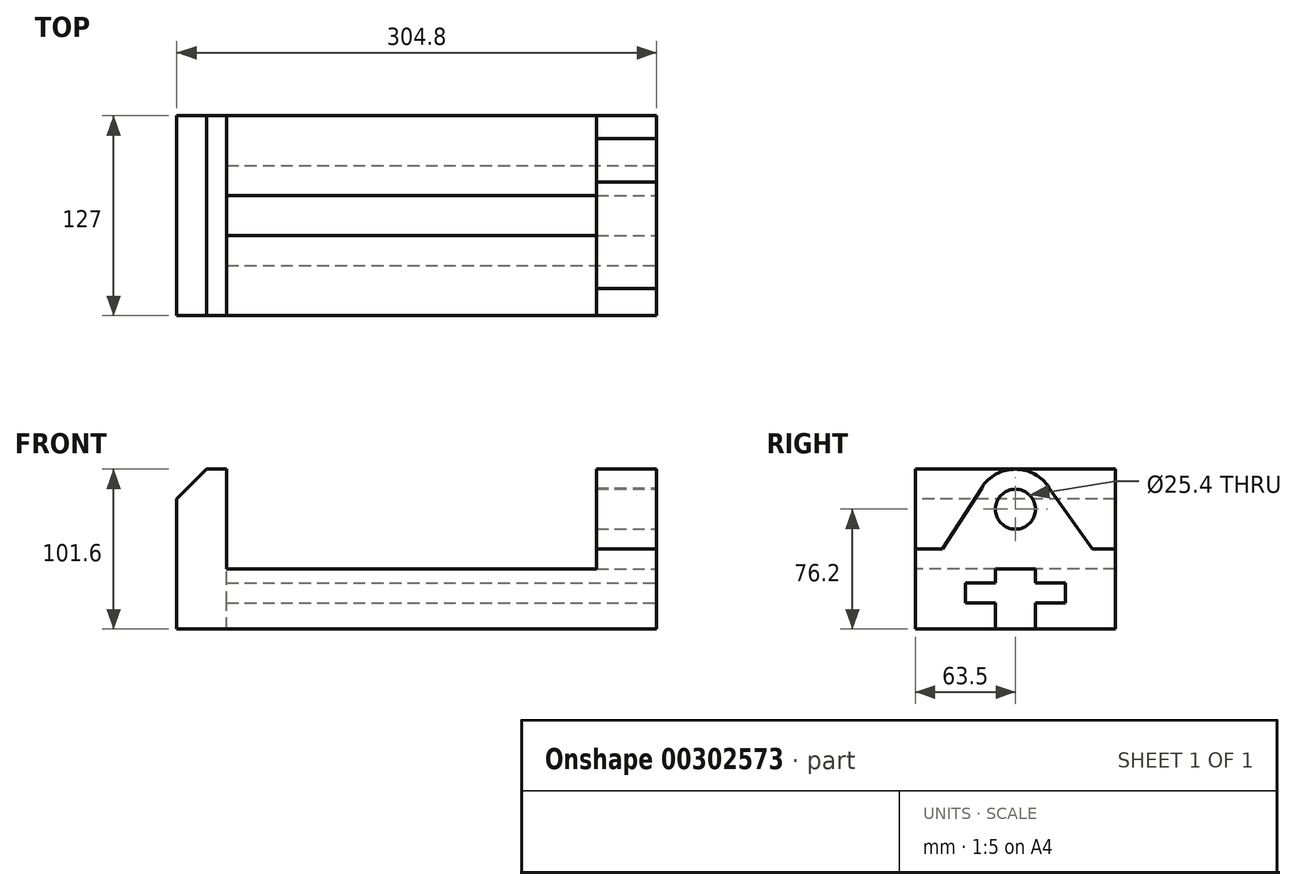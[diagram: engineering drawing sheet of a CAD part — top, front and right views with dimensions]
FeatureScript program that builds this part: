
annotation { "Feature Type Name" : "Feature", "Feature Type Description" : "" }
export const myFeature = defineFeature(function(context is Context, id is Id, definition is map)
    precondition{}
    {
        {
            var Q0;
            Q0=qCreatedBy(makeId("Front.planeOp"),FACE);
            var sketch = newSketch(context, id + "F0", { "sketchPlane" : qUnion([Q0])});
            skLineSegment(sketch, "E0.bottom", {"start": v(0, 0) * mm, "end": v(304.8, 0) * mm});
            skLineSegment(sketch, "E0.top", {"start": v(0, 101.6) * mm, "end": v(304.8, 101.6) * mm});
            skLineSegment(sketch, "E0.left", {"start": v(0, 0) * mm, "end": v(0, 101.6) * mm});
            skLineSegment(sketch, "E0.right", {"start": v(304.8, 0) * mm, "end": v(304.8, 101.6) * mm});
            skSolve(sketch);
        }
        {
            var Q0;
            Q0 = qSketchRegion(id + "F0", true);
            extrude(context, id + "F1", {"entities" : qUnion([Q0]), "oppositeDirection" : true, "depth" : 127 * mm});
        }
        {
            var Q0;
            Q0=makeQuery(id+"F1.opExtrude","CAP_FACE",FACE,{"disambiguationData":[OSD([sQuery(id+"F0.wireOp",EDGE,"E0.bottom"),sQuery(id+"F0.wireOp",EDGE,"E0.top"),sQuery(id+"F0.wireOp",EDGE,"E0.left"),sQuery(id+"F0.wireOp",EDGE,"E0.right")])],"isStart":true});
            var sketch = newSketch(context, id + "F2", { "sketchPlane" : qUnion([Q0])});
            skLineSegment(sketch, "E1", {"start": v(0, 101.6) * mm, "end": v(31.75, 101.6) * mm});
            skLineSegment(sketch, "E2", {"start": v(304.8, 101.6) * mm, "end": v(266.7, 101.6) * mm});
            skLineSegment(sketch, "E3", {"start": v(0, 38.1) * mm, "end": v(304.8, 38.1) * mm, "construction": true});
            skLineSegment(sketch, "E4", {"start": v(31.75, 101.6) * mm, "end": v(31.75, 38.1) * mm});
            skLineSegment(sketch, "E5", {"start": v(31.75, 38.1) * mm, "end": v(266.7, 38.1) * mm});
            skLineSegment(sketch, "E6", {"start": v(266.7, 38.1) * mm, "end": v(266.7, 101.6) * mm});
            skSolve(sketch);
        }
        {
            var Q0;
            {var subQ0=sQuery(id+"F2.wireOp",EDGE,"E4");Q0=makeQuery(id+"F2.imprint","IMPRINT",FACE,{"disambiguationData":[TD([[makeQuery(id+"F2.imprint","IMPRINT",EDGE,{"derivedFrom":subQ0}),1.0]])]});}
            extrude(context, id + "F3", {"entities" : qUnion([Q0]), "operationType" : NewBodyOperationType.REMOVE, "endBound" : BoundingType.THROUGH_ALL, "oppositeDirection" : true, "depth" : 25.4 * mm});
        }
        {
            var Q0;
            Q0=makeQuery(id+"F1.opExtrude","CAP_FACE",FACE,{"disambiguationData":[OSD([sQuery(id+"F0.wireOp",EDGE,"E0.bottom"),sQuery(id+"F0.wireOp",EDGE,"E0.top"),sQuery(id+"F0.wireOp",EDGE,"E0.left"),sQuery(id+"F0.wireOp",EDGE,"E0.right")])],"isStart":true});
            var sketch = newSketch(context, id + "F4", { "sketchPlane" : qUnion([Q0])});
            skLineSegment(sketch, "E7", {"start": v(0, 101.6) * mm, "end": v(19.05, 101.6) * mm});
            skLineSegment(sketch, "E8", {"start": v(0, 101.6) * mm, "end": v(0, 82.55) * mm});
            skLineSegment(sketch, "E9", {"start": v(0, 82.55) * mm, "end": v(19.05, 101.6) * mm});
            skSolve(sketch);
        }
        {
            var Q0;
            Q0 = qSketchRegion(id + "F4", true);
            extrude(context, id + "F5", {"entities" : qUnion([Q0]), "operationType" : NewBodyOperationType.REMOVE, "endBound" : BoundingType.THROUGH_ALL, "oppositeDirection" : true, "depth" : 25.4 * mm});
        }
        {
            var Q0;
            Q0=makeQuery(id+"F1.opExtrude","SWEPT_FACE",FACE,{"disambiguationData":[OSD([sQuery(id+"F0.wireOp",EDGE,"E0.right")])]});
            var sketch = newSketch(context, id + "F6", { "sketchPlane" : qUnion([Q0])});
            skLineSegment(sketch, "E10", {"start": v(0, 50.8) * mm, "end": v(17.22, 50.8) * mm});
            skLineSegment(sketch, "E11", {"start": v(127, 50.8) * mm, "end": v(112.47, 50.8) * mm});
            skLineSegment(sketch, "E12", {"start": v(63.5, 101.6) * mm, "end": v(63.5, 0) * mm, "construction": true});
            skLineSegment(sketch, "E13", {"start": v(50.8, 0) * mm, "end": v(50.8, 16.51) * mm});
            skLineSegment(sketch, "E14", {"start": v(50.8, 16.51) * mm, "end": v(31.75, 16.51) * mm});
            skLineSegment(sketch, "E15", {"start": v(31.75, 16.51) * mm, "end": v(31.75, 29.21) * mm});
            skLineSegment(sketch, "E16", {"start": v(31.75, 29.21) * mm, "end": v(50.8, 29.21) * mm});
            skLineSegment(sketch, "E17", {"start": v(50.8, 29.21) * mm, "end": v(50.8, 38.1) * mm});
            skLineSegment(sketch, "E18", {"start": v(50.8, 38.1) * mm, "end": v(63.5, 38.1) * mm});
            skLineSegment(sketch, "E19", {"start": v(50.8, 0) * mm, "end": v(63.5, 0) * mm});
            skLineSegment(sketch, "E20", {"start": v(63.5, 38.1) * mm, "end": v(76.2, 38.1) * mm});
            skLineSegment(sketch, "E21", {"start": v(76.2, 38.1) * mm, "end": v(76.2, 29.21) * mm});
            skLineSegment(sketch, "E22", {"start": v(76.2, 29.21) * mm, "end": v(95.25, 29.21) * mm});
            skLineSegment(sketch, "E23", {"start": v(95.25, 29.21) * mm, "end": v(95.25, 16.51) * mm});
            skLineSegment(sketch, "E24", {"start": v(95.25, 16.51) * mm, "end": v(76.2, 16.51) * mm});
            skLineSegment(sketch, "E25", {"start": v(76.2, 16.51) * mm, "end": v(76.2, 0) * mm});
            skLineSegment(sketch, "E26", {"start": v(76.2, 0) * mm, "end": v(63.5, 0) * mm});
            skCircle(sketch, "E27", {"center": v(63.5, 76.2) * mm, "radius": 12.7 * mm});
            skArc(sketch, "E28", {"start": v(84.93, 89.84) * mm, "mid": v(63.5, 101.6) * mm, "end": v(42.07, 89.84) * mm});
            skLineSegment(sketch, "E29", {"start": v(17.22, 50.8) * mm, "end": v(42.07, 89.84) * mm});
            skLineSegment(sketch, "E30", {"start": v(84.93, 89.84) * mm, "end": v(112.47, 50.8) * mm});
            skSolve(sketch);
        }
        {
            var Q0;
            {var subQ7=sQuery(id+"F6.wireOp",EDGE,"E10");Q0=makeQuery(id+"F6.imprint","IMPRINT",FACE,{"disambiguationData":[TD([[makeQuery(id+"F6.imprint","IMPRINT",EDGE,{"derivedFrom":subQ7}),1.0]])]});}
            var Q1;
            {var subQ7=sQuery(id+"F6.wireOp",EDGE,"E11");Q1=makeQuery(id+"F6.imprint","IMPRINT",FACE,{"disambiguationData":[TD([[makeQuery(id+"F6.imprint","IMPRINT",EDGE,{"derivedFrom":subQ7}),-1.0]])]});}
            var Q2;
            Q2=makeQuery(id+"F6.imprint","IMPRINT",FACE,{"disambiguationData":[TD([[makeQuery(id+"F6.imprint","IMPRINT",EDGE,{"derivedFrom":sQuery(id+"F6.wireOp",EDGE,"E27")}),1.0]])]});
            extrude(context, id + "F7", {"entities" : qUnion([Q0, Q1, Q2]), "operationType" : NewBodyOperationType.REMOVE, "endBound" : BoundingType.UP_TO_NEXT, "oppositeDirection" : true, "depth" : 25.4 * mm});
        }
        {
            var Q0;
            Q0=makeQuery(id+"F6.imprint","IMPRINT",FACE,{"disambiguationData":[TD([[makeQuery(id+"F6.imprint","IMPRINT",EDGE,{"derivedFrom":sQuery(id+"F6.wireOp",EDGE,"E13")}),-1.0]])]});
            extrude(context, id + "F8", {"entities" : qUnion([Q0]), "operationType" : NewBodyOperationType.REMOVE, "oppositeDirection" : true, "depth" : 273.05 * mm});
        }
    });
